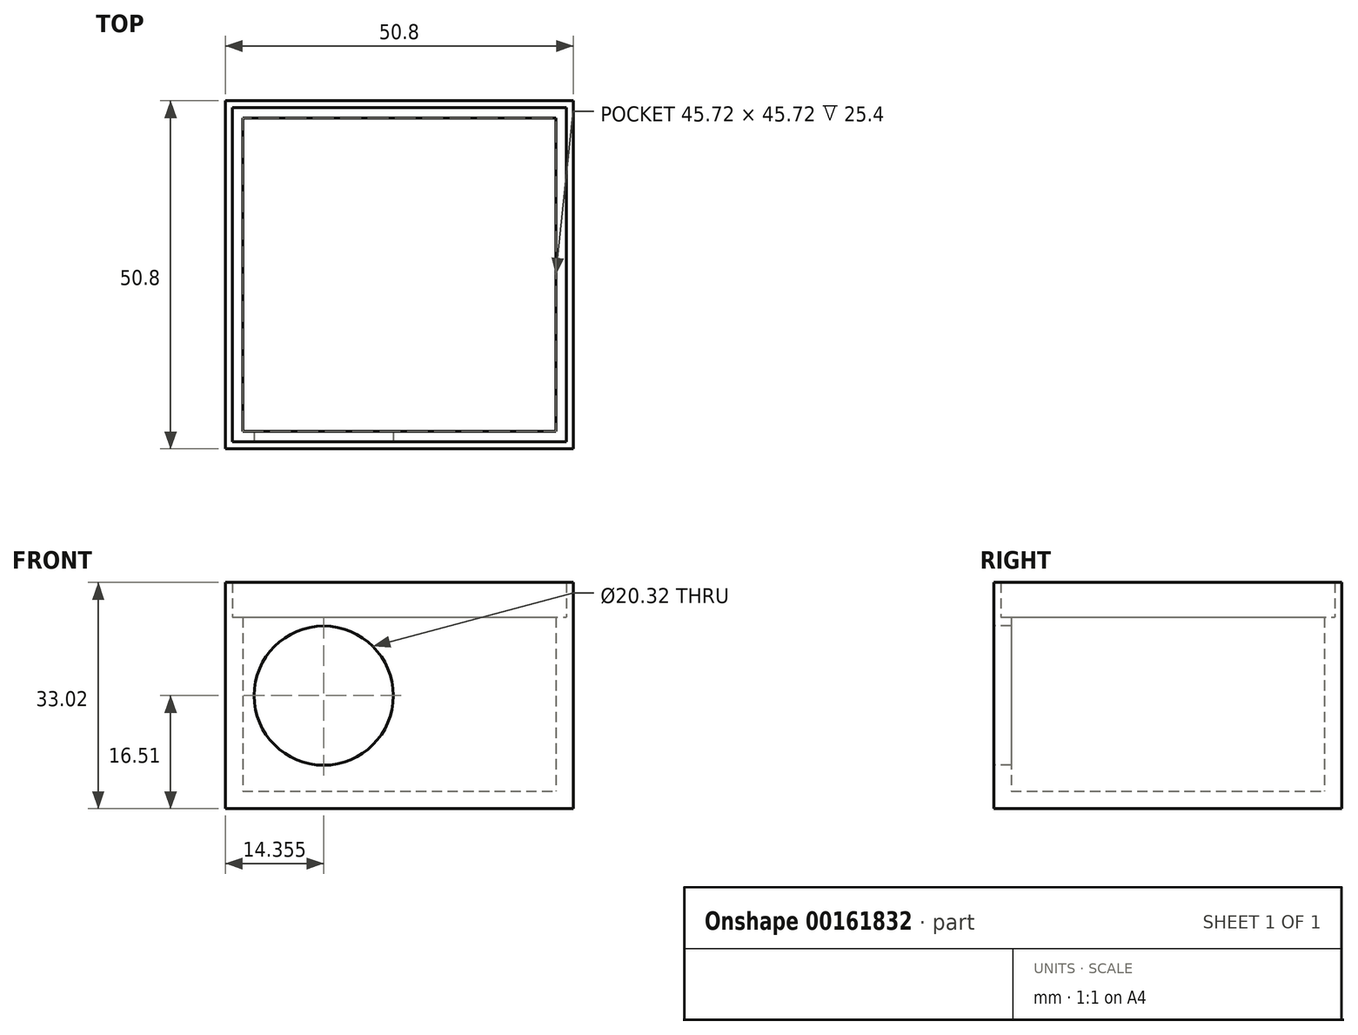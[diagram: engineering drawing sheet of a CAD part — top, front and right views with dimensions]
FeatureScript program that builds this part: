
annotation { "Feature Type Name" : "Feature", "Feature Type Description" : "" }
export const myFeature = defineFeature(function(context is Context, id is Id, definition is map)
    precondition{}
    {
        {
            var Q0;
            Q0=qCreatedBy(makeId("Top.planeOp"),FACE);
            var sketch = newSketch(context, id + "F0", { "sketchPlane" : qUnion([Q0])});
            skLineSegment(sketch, "E0.bottom", {"start": v(0, 0) * mm, "end": v(50.8, 0) * mm});
            skLineSegment(sketch, "E0.top", {"start": v(0, 50.8) * mm, "end": v(50.8, 50.8) * mm});
            skLineSegment(sketch, "E0.left", {"start": v(0, 0) * mm, "end": v(0, 50.8) * mm});
            skLineSegment(sketch, "E0.right", {"start": v(50.8, 0) * mm, "end": v(50.8, 50.8) * mm});
            skSolve(sketch);
        }
        {
            var Q0;
            Q0 = qSketchRegion(id + "F0", true);
            extrude(context, id + "F1", {"entities" : qUnion([Q0]), "depth" : 2.54 * mm});
        }
        {
            var Q0;
            Q0=makeQuery(id+"F1.opExtrude","CAP_FACE",FACE,{"disambiguationData":[OSD([sQuery(id+"F0.wireOp",EDGE,"E0.bottom"),sQuery(id+"F0.wireOp",EDGE,"E0.top"),sQuery(id+"F0.wireOp",EDGE,"E0.left"),sQuery(id+"F0.wireOp",EDGE,"E0.right")])],"isStart":false});
            var sketch = newSketch(context, id + "F2", { "sketchPlane" : qUnion([Q0])});
            skLineSegment(sketch, "E1.bottom", {"start": v(0, 0) * mm, "end": v(50.8, 0) * mm});
            skLineSegment(sketch, "E1.top", {"start": v(0, 50.8) * mm, "end": v(50.8, 50.8) * mm});
            skLineSegment(sketch, "E1.left", {"start": v(0, 0) * mm, "end": v(0, 50.8) * mm});
            skLineSegment(sketch, "E1.right", {"start": v(50.8, 0) * mm, "end": v(50.8, 50.8) * mm});
            skLineSegment(sketch, "E2.0", {"start": v(1.02, 49.78) * mm, "end": v(49.78, 49.78) * mm});
            skLineSegment(sketch, "E2.1", {"start": v(1.02, 1.02) * mm, "end": v(1.02, 49.78) * mm});
            skLineSegment(sketch, "E2.2", {"start": v(1.02, 1.02) * mm, "end": v(49.78, 1.02) * mm});
            skLineSegment(sketch, "E2.3", {"start": v(49.78, 1.02) * mm, "end": v(49.78, 49.78) * mm});
            skSolve(sketch);
        }
        {
            var Q0;
            Q0 = qSketchRegion(id + "F2", true);
            extrude(context, id + "F3", {"entities" : qUnion([Q0]), "operationType" : NewBodyOperationType.ADD, "depth" : 30.48 * mm});
        }
        {
            var Q0;
            Q0=makeQuery(id+"F1.opExtrude","CAP_FACE",FACE,{"disambiguationData":[OSD([sQuery(id+"F0.wireOp",EDGE,"E0.bottom"),sQuery(id+"F0.wireOp",EDGE,"E0.top"),sQuery(id+"F0.wireOp",EDGE,"E0.left"),sQuery(id+"F0.wireOp",EDGE,"E0.right")])],"isStart":false});
            var sketch = newSketch(context, id + "F4", { "sketchPlane" : qUnion([Q0])});
            skLineSegment(sketch, "E3.bottom", {"start": v(0, 0) * mm, "end": v(50.8, 0) * mm});
            skLineSegment(sketch, "E3.top", {"start": v(0, 50.8) * mm, "end": v(50.8, 50.8) * mm});
            skLineSegment(sketch, "E3.left", {"start": v(0, 0) * mm, "end": v(0, 50.8) * mm});
            skLineSegment(sketch, "E3.right", {"start": v(50.8, 0) * mm, "end": v(50.8, 50.8) * mm});
            skLineSegment(sketch, "E4.0", {"start": v(2.54, 48.26) * mm, "end": v(48.26, 48.26) * mm});
            skLineSegment(sketch, "E4.1", {"start": v(2.54, 2.54) * mm, "end": v(2.54, 48.26) * mm});
            skLineSegment(sketch, "E4.2", {"start": v(2.54, 2.54) * mm, "end": v(48.26, 2.54) * mm});
            skLineSegment(sketch, "E4.3", {"start": v(48.26, 2.54) * mm, "end": v(48.26, 48.26) * mm});
            skLineSegment(sketch, "E5.bottom", {"start": v(1.02, 1.02) * mm, "end": v(49.78, 1.02) * mm});
            skLineSegment(sketch, "E5.top", {"start": v(1.02, 49.78) * mm, "end": v(49.78, 49.78) * mm});
            skLineSegment(sketch, "E5.left", {"start": v(1.02, 1.02) * mm, "end": v(1.02, 49.78) * mm});
            skLineSegment(sketch, "E5.right", {"start": v(49.78, 1.02) * mm, "end": v(49.78, 49.78) * mm});
            skSolve(sketch);
        }
        {
            var Q0;
            Q0 = qSketchRegion(id + "F4", true);
            var Q1;
            Q1=makeQuery(id+"F4.imprint","IMPRINT",FACE,{"disambiguationData":[TD([[makeQuery(id+"F4.imprint","IMPRINT",EDGE,{"derivedFrom":sQuery(id+"F4.wireOp",EDGE,"E4.0")}),1.0]])]});
            extrude(context, id + "F5", {"entities" : qUnion([Q0, Q1]), "operationType" : NewBodyOperationType.ADD, "depth" : 25.4 * mm});
        }
        {
            var Q0;
            Q0=makeQuery(id+"F3.boolean.opBoolean","MERGE",FACE,{"derivedFrom":[makeQuery(id+"F1.opExtrude","SWEPT_FACE",FACE,{"disambiguationData":[OSD([sQuery(id+"F0.wireOp",EDGE,"E0.bottom")])]}),makeQuery(id+"F3.opExtrude","SWEPT_FACE",FACE,{"disambiguationData":[OSD([sQuery(id+"F2.wireOp",EDGE,"E1.bottom")])]})]});
            var sketch = newSketch(context, id + "F6", { "sketchPlane" : qUnion([Q0])});
            skCircle(sketch, "E6", {"center": v(14.35, 16.51) * mm, "radius": 10.16 * mm});
            skPoint(sketch, "E6.centerSnap0", {"position": v(0, 16.51) * mm});
            skSolve(sketch);
        }
        {
            var Q0;
            Q0 = qSketchRegion(id + "F6", true);
            extrude(context, id + "F7", {"entities" : qUnion([Q0]), "operationType" : NewBodyOperationType.REMOVE, "oppositeDirection" : true, "depth" : 25.4 * mm});
        }
    });
